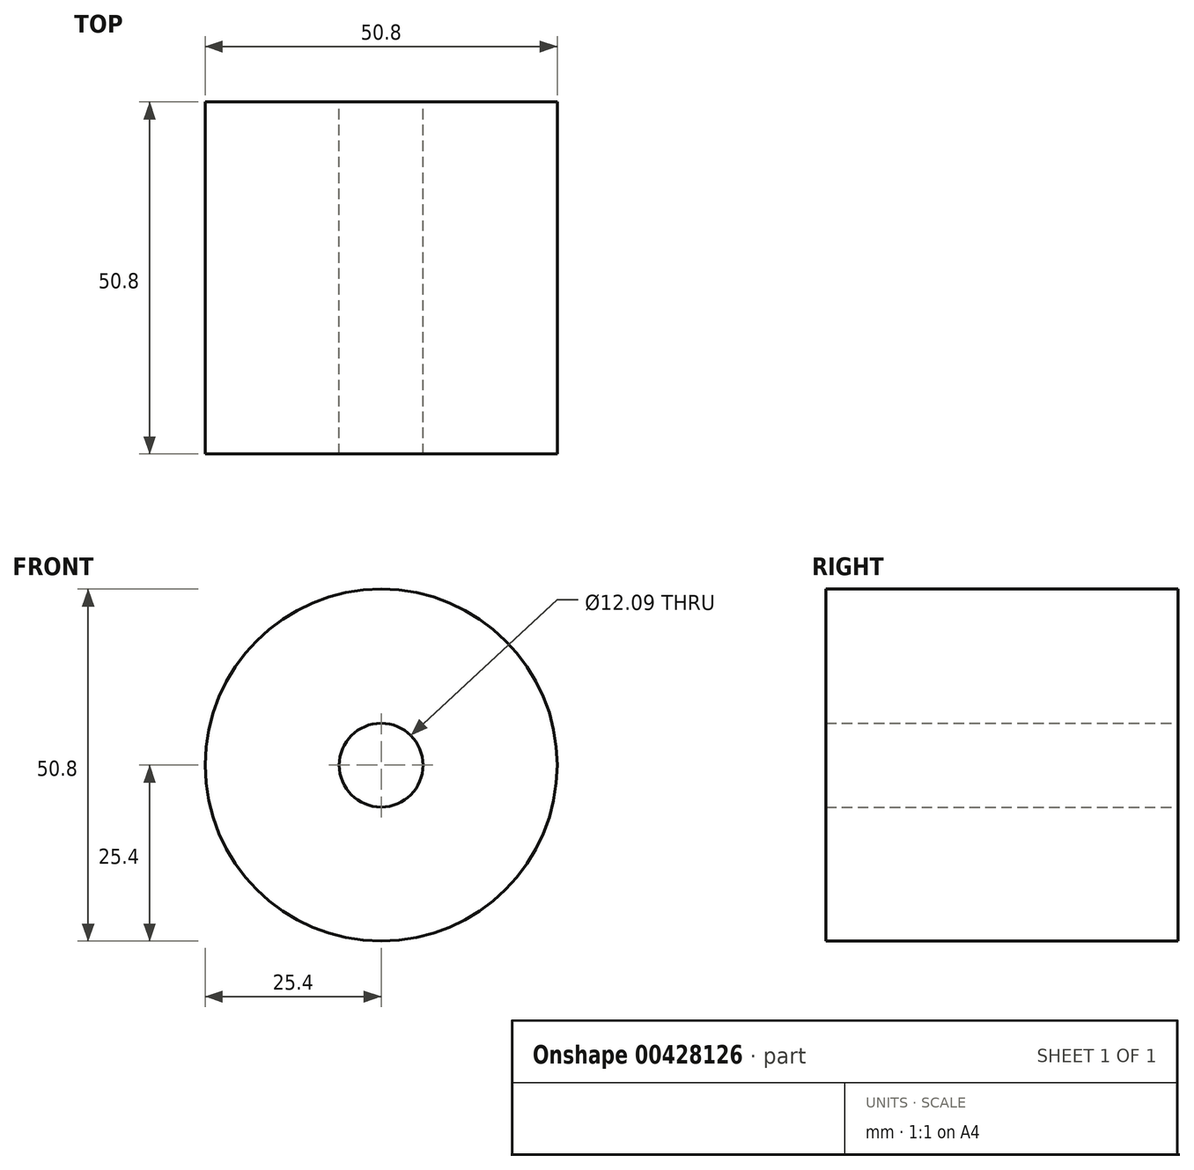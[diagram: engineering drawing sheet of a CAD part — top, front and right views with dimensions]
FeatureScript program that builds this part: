
annotation { "Feature Type Name" : "Feature", "Feature Type Description" : "" }
export const myFeature = defineFeature(function(context is Context, id is Id, definition is map)
    precondition{}
    {
        {
            var Q0;
            Q0=qCreatedBy(makeId("Front.planeOp"),FACE);
            var sketch = newSketch(context, id + "F0", { "sketchPlane" : qUnion([Q0])});
            skCircle(sketch, "E0", {"center": v(0, 0) * mm, "radius": 25.4 * mm});
            skCircle(sketch, "E1", {"center": v(0, 0) * mm, "radius": 6.05 * mm});
            skSolve(sketch);
        }
        {
            var Q0;
            Q0=makeQuery(id+"F0.imprint","IMPRINT",FACE,{"disambiguationData":[TD([[makeQuery(id+"F0.imprint","IMPRINT",EDGE,{"derivedFrom":sQuery(id+"F0.wireOp",EDGE,"E0")}),1.0]])]});
            extrude(context, id + "F1", {"entities" : qUnion([Q0]), "depth" : 50.8 * mm});
        }
    });
